# Revit family: Sink-Bathroom_Vessel-KOHLER-Chord-K-2331
name_source: partatom
category: Plumbing Fixtures
revit_build: Autodesk Revit 2015 (Build: 20140606_1530(x64)
units: mm (PartAtom-declared; Revit-internal decimal feet)

## types (6) — shared parameters
ADA Compliant = No
Assembly Code = D2010400
Cold Water Inlet = Cold Water Inlet
Date Modified = 12/13/2017
Default Elevation = 36"
Height = 4 3/16"
Hot Water Inlet = Hot Water Inlet
Length = 16 13/16"
Manufacturer = KOHLER Co.
MasterFormat 1995 = 15410
MasterFormat 2004 = 22.41.16
Material = Vitreous China
Product Documentation Link = http://www.us.kohler.com
Product Name = Chord
Product Page URL = http://www.us.kohler.com
URL = https://www.us.kohler.com
Waste Connection = Yes
Waste Water Outlet = Waste Water Outlet
Width = 18 5/8"

## per-type parameters (varying)
| type | 2331_8 | Description | Finish | Model | Type |
| Single faucet hole, 0-White | No | Wading Pool bathroom sink with single faucet hole | Kohler-Vitreous_China-0-White | K-2331-1-0 | 1 |
| Single faucet hole, 96-Biscuit | No | Wading Pool bathroom sink with single faucet hole | Kohler-Vitreous_China-96-Biscuit | K-2331-1-96 | 2 |
| Single faucet hole, 47-Almond | No | Wading Pool bathroom sink with single faucet hole | Kohler-Vitreous_China-47-Almond | K-2331-1-47 | 3 |
| 8" widespread faucet holes, 0-White | Yes | Wading Pool bathroom sink with 8inch widespread faucet holes | Kohler-Vitreous_China-0-White | K-2331-8-0 | 4 |
| 8" widespread faucet holes, 96-Biscuit | Yes | Wading Pool bathroom sink with 8inch widespread faucet holes | Kohler-Vitreous_China-96-Biscuit | K-2331-8-96 | 5 |
| 8" widespread faucet holes, 47-Almond | Yes | Wading Pool bathroom sink with 8inch widespread faucet holes | Kohler-Vitreous_China-47-Almond | K-2331-8-47 | 6 |

## geometry (parser evidence)
native form markers: Sweep x6
no freeform markers — native parametric forms only
